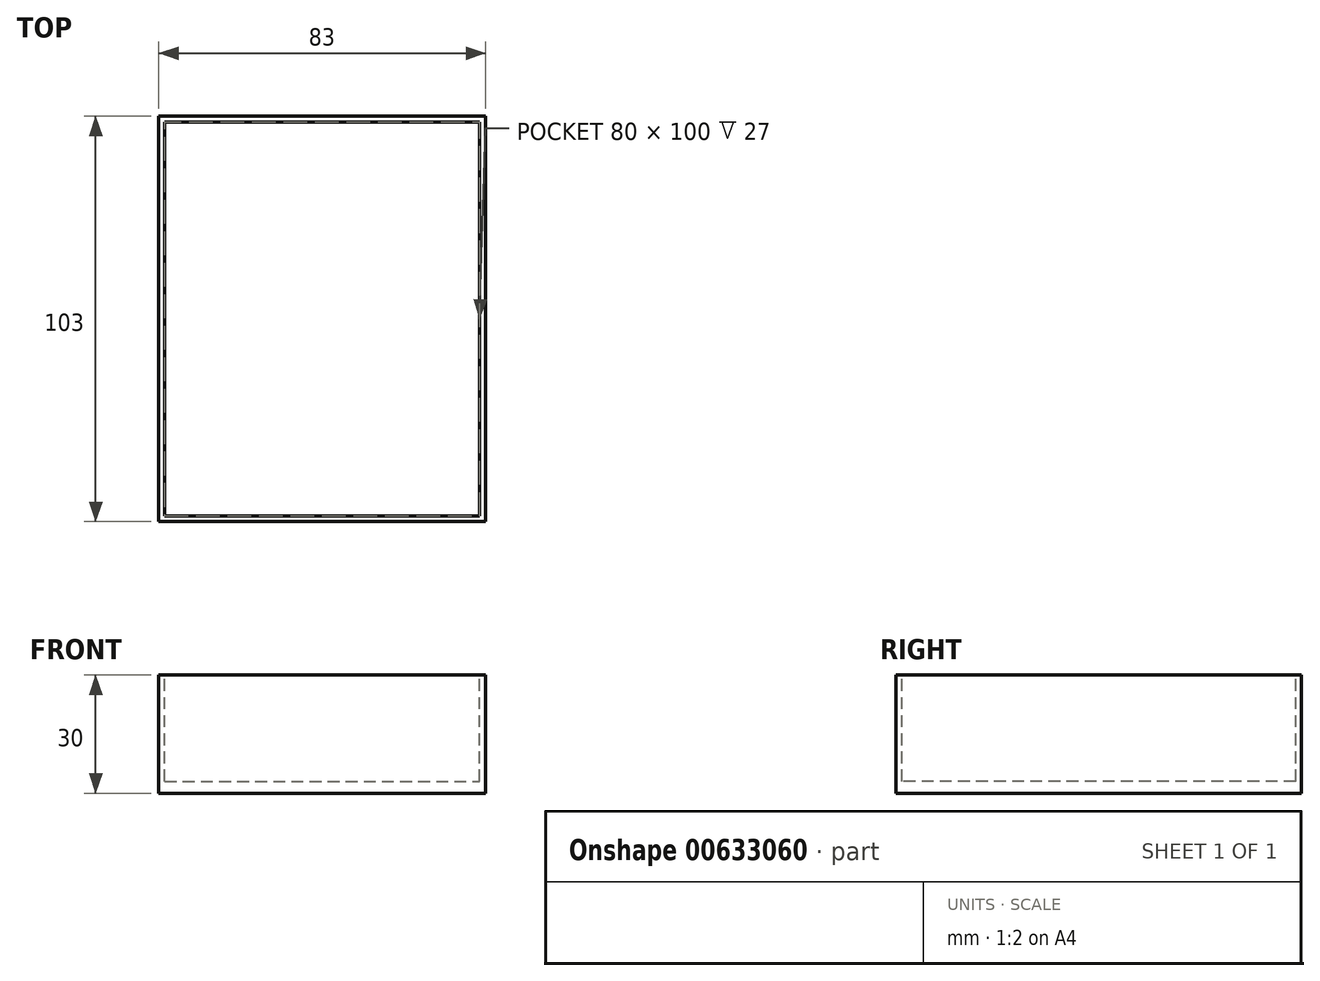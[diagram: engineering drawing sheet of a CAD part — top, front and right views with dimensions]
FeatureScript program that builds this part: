
annotation { "Feature Type Name" : "Feature", "Feature Type Description" : "" }
export const myFeature = defineFeature(function(context is Context, id is Id, definition is map)
    precondition{}
    {
        {
            var Q0;
            Q0=qCreatedBy(makeId("Top.planeOp"),FACE);
            var sketch = newSketch(context, id + "F0", { "sketchPlane" : qUnion([Q0])});
            skLineSegment(sketch, "E0.bottom", {"start": v(-41.5, 51.5) * mm, "end": v(41.5, 51.5) * mm});
            skLineSegment(sketch, "E0.top", {"start": v(-41.5, -51.5) * mm, "end": v(41.5, -51.5) * mm});
            skLineSegment(sketch, "E0.left", {"start": v(-41.5, 51.5) * mm, "end": v(-41.5, -51.5) * mm});
            skLineSegment(sketch, "E0.right", {"start": v(41.5, 51.5) * mm, "end": v(41.5, -51.5) * mm});
            skPoint(sketch, "E0.middle", {"position": v(0, 0) * mm});
            skSolve(sketch);
        }
        {
            var Q0;
            Q0 = qSketchRegion(id + "F0", true);
            extrude(context, id + "F1", {"entities" : qUnion([Q0]), "oppositeDirection" : true, "depth" : 30 * mm, "offsetDistance" : 25 * mm});
        }
        {
            var Q0;
            Q0=qCreatedBy(makeId("Top.planeOp"),FACE);
            var sketch = newSketch(context, id + "F2", { "sketchPlane" : qUnion([Q0])});
            skLineSegment(sketch, "E1.bottom", {"start": v(-40, 50) * mm, "end": v(40, 50) * mm});
            skLineSegment(sketch, "E1.top", {"start": v(-40, -50) * mm, "end": v(40, -50) * mm});
            skLineSegment(sketch, "E1.left", {"start": v(-40, 50) * mm, "end": v(-40, -50) * mm});
            skLineSegment(sketch, "E1.right", {"start": v(40, 50) * mm, "end": v(40, -50) * mm});
            skPoint(sketch, "E1.middle", {"position": v(0, 0) * mm});
            skSolve(sketch);
        }
        {
            var Q0;
            Q0 = qSketchRegion(id + "F2", true);
            extrude(context, id + "F3", {"entities" : qUnion([Q0]), "operationType" : NewBodyOperationType.REMOVE, "oppositeDirection" : true, "depth" : 27 * mm, "offsetDistance" : 25 * mm});
        }
    });
